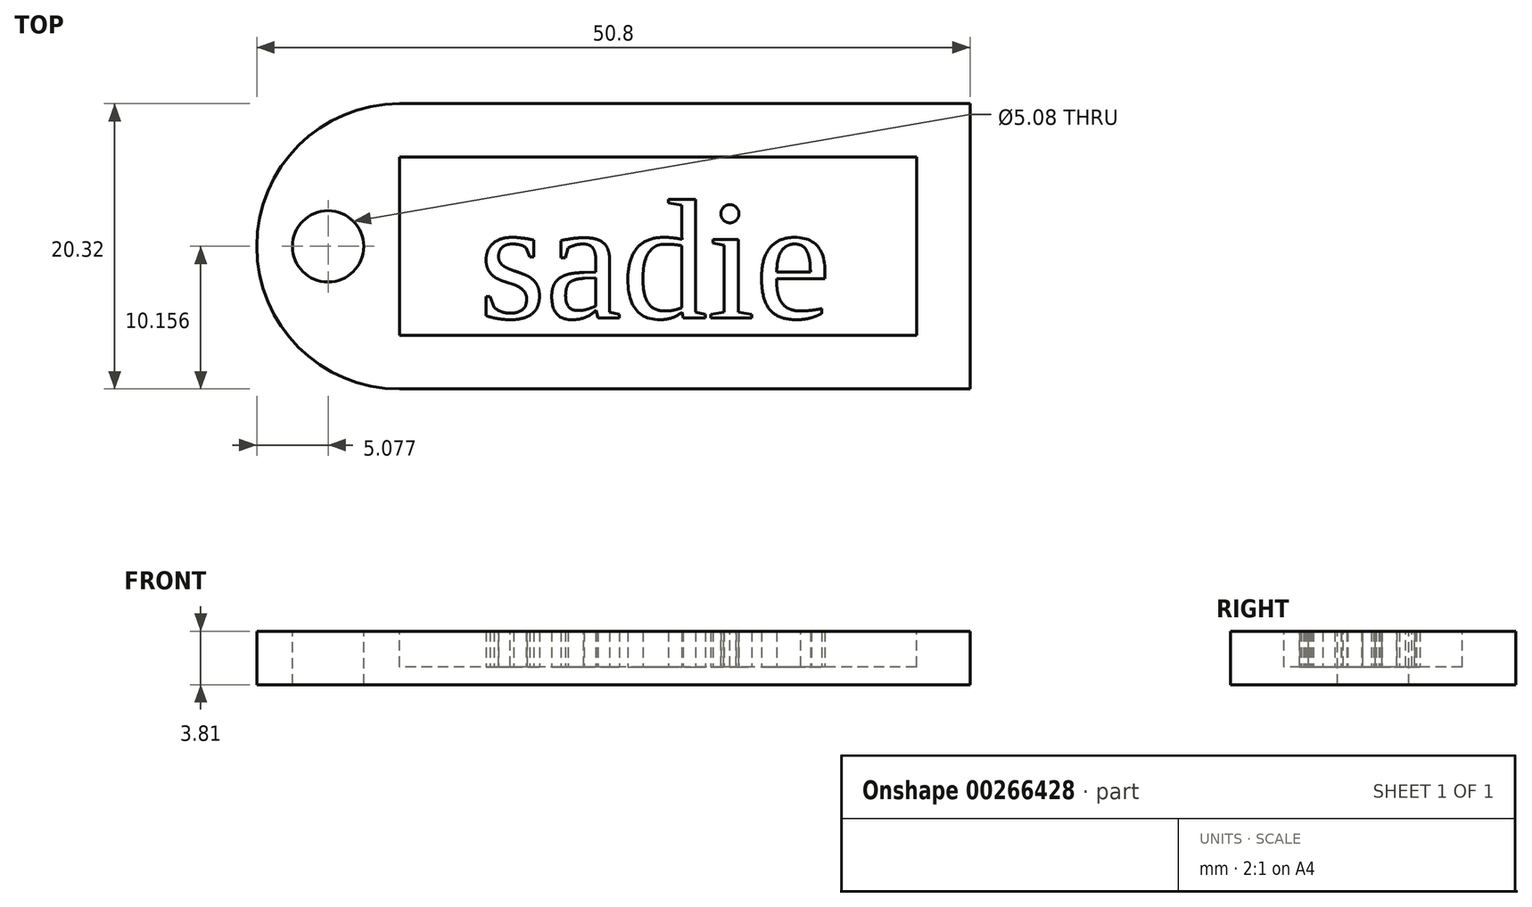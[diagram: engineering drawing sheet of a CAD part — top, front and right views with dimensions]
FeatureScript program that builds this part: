
annotation { "Feature Type Name" : "Feature", "Feature Type Description" : "" }
export const myFeature = defineFeature(function(context is Context, id is Id, definition is map)
    precondition{}
    {
        {
            var Q0;
            Q0=qCreatedBy(makeId("Top.planeOp"),FACE);
            var sketch = newSketch(context, id + "F0", { "sketchPlane" : qUnion([Q0])});
            skLineSegment(sketch, "E0.bottom", {"start": v(-22.33, 27.99) * mm, "end": v(18.3, 27.99) * mm});
            skLineSegment(sketch, "E0.top", {"start": v(-22.33, 48.3) * mm, "end": v(18.3, 48.3) * mm});
            skLineSegment(sketch, "E0.left", {"start": v(-32.5, 38.15) * mm, "end": v(-32.5, 38.15) * mm});
            skLineSegment(sketch, "E0.right", {"start": v(18.3, 27.99) * mm, "end": v(18.3, 48.3) * mm});
            skPoint(sketch, "E1.visualSharp", {"position": v(-32.5, 48.3) * mm});
            skArc(sketch, "E1.filletArc", {"start": v(-22.33, 48.3) * mm, "mid": v(-29.52, 45.33) * mm, "end": v(-32.5, 38.15) * mm});
            skPoint(sketch, "E2.visualSharp", {"position": v(-32.5, 27.99) * mm});
            skArc(sketch, "E2.filletArc", {"start": v(-32.5, 38.15) * mm, "mid": v(-29.52, 30.96) * mm, "end": v(-22.33, 27.99) * mm});
            skSolve(sketch);
        }
        {
            var Q0;
            Q0=makeQuery(id+"F0.imprint","IMPRINT",FACE,{"disambiguationData":[TD([[makeQuery(id+"F0.imprint","IMPRINT",EDGE,{"derivedFrom":sQuery(id+"F0.wireOp",EDGE,"E0.bottom")}),1.0]])]});
            extrude(context, id + "F1", {"entities" : qUnion([Q0]), "depth" : 3.8 * mm});
        }
        {
            var Q0;
            Q0=makeQuery(id+"F1.opExtrude","CAP_FACE",FACE,{"disambiguationData":[OSD([sQuery(id+"F0.wireOp",EDGE,"E0.bottom"),sQuery(id+"F0.wireOp",EDGE,"E0.top"),sQuery(id+"F0.wireOp",EDGE,"E0.right"),sQuery(id+"F0.wireOp",EDGE,"E1.filletArc"),sQuery(id+"F0.wireOp",EDGE,"E2.filletArc")])],"isStart":false});
            var sketch = newSketch(context, id + "F2", { "sketchPlane" : qUnion([Q0])});
            skPoint(sketch, "E3", {"position": v(-22.33, 31.8) * mm});
            skPoint(sketch, "E4", {"position": v(14.5, 44.5) * mm});
            skLineSegment(sketch, "E5.bottom", {"start": v(14.5, 44.5) * mm, "end": v(-22.33, 44.5) * mm});
            skLineSegment(sketch, "E5.top", {"start": v(14.5, 31.8) * mm, "end": v(-22.33, 31.8) * mm});
            skLineSegment(sketch, "E5.left", {"start": v(14.5, 44.5) * mm, "end": v(14.5, 31.8) * mm});
            skLineSegment(sketch, "E5.right", {"start": v(-22.33, 44.5) * mm, "end": v(-22.33, 31.8) * mm});
            skSolve(sketch);
        }
        {
            var Q0;
            Q0 = qSketchRegion(id + "F2", true);
            extrude(context, id + "F3", {"entities" : qUnion([Q0]), "operationType" : NewBodyOperationType.REMOVE, "oppositeDirection" : true, "depth" : 2.54 * mm});
        }
        {
            var Q0;
            Q0=makeQuery(id+"F1.opExtrude","CAP_FACE",FACE,{"disambiguationData":[OSD([sQuery(id+"F0.wireOp",EDGE,"E0.bottom"),sQuery(id+"F0.wireOp",EDGE,"E0.top"),sQuery(id+"F0.wireOp",EDGE,"E0.right"),sQuery(id+"F0.wireOp",EDGE,"E1.filletArc"),sQuery(id+"F0.wireOp",EDGE,"E2.filletArc")])],"isStart":false});
            var sketch = newSketch(context, id + "F4", { "sketchPlane" : qUnion([Q0])});
            skPoint(sketch, "E6", {"position": v(-32.5, 38.15) * mm});
            skPoint(sketch, "E7", {"position": v(-27.41, 38.15) * mm});
            skPoint(sketch, "E8", {"position": v(-48.38, 58.73) * mm});
            skCircle(sketch, "E9", {"center": v(-27.41, 38.15) * mm, "radius": 2.54 * mm});
            skSolve(sketch);
        }
        {
            var Q0;
            Q0 = qSketchRegion(id + "F4", true);
            extrude(context, id + "F5", {"entities" : qUnion([Q0]), "operationType" : NewBodyOperationType.REMOVE, "oppositeDirection" : true, "depth" : 25.4 * mm});
        }
        {
            var Q0;
            Q0=makeQuery(id+"F3.boolean.opBoolean","COPY",FACE,{"derivedFrom":makeQuery(id+"F3.opExtrude","CAP_FACE",FACE,{"disambiguationData":[OSD([sQuery(id+"F2.wireOp",EDGE,"E5.bottom"),sQuery(id+"F2.wireOp",EDGE,"E5.top"),sQuery(id+"F2.wireOp",EDGE,"E5.left"),sQuery(id+"F2.wireOp",EDGE,"E5.right")])],"isStart":false})});
            var sketch = newSketch(context, id + "F6", { "sketchPlane" : qUnion([Q0])});
            skText(sketch, "E10", { "text": "sadie", "fontName": "Tinos-Regular.ttf"});
            const initialGuessF6  = {"E10": [-0.01666, 0.03304, 1, 0, 0.00878]};
            skSetInitialGuess(sketch, initialGuessF6);
            skSolve(sketch);
        }
        {
            var Q0;
            Q0 = qSketchRegion(id + "F6", true);
            extrude(context, id + "F7", {"entities" : qUnion([Q0]), "operationType" : NewBodyOperationType.ADD, "depth" : 2.54 * mm});
        }
    });
